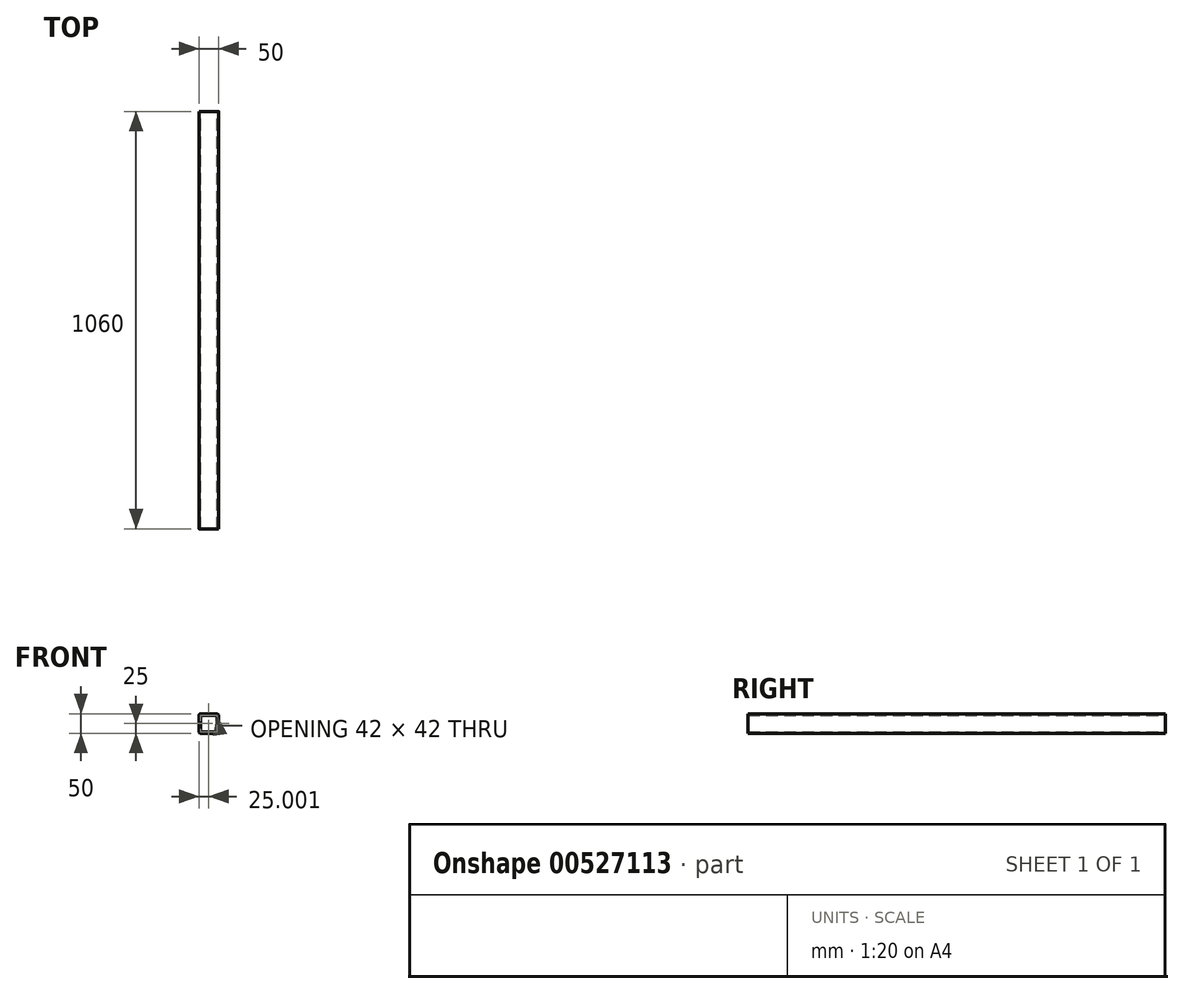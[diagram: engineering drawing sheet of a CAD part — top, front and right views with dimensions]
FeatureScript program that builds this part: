
annotation { "Feature Type Name" : "Feature", "Feature Type Description" : "" }
export const myFeature = defineFeature(function(context is Context, id is Id, definition is map)
    precondition{}
    {
        {
            var Q0;
            Q0=qCreatedBy(makeId("Front.planeOp"),FACE);
            var sketch = newSketch(context, id + "F0", { "sketchPlane" : qUnion([Q0])});
            skLineSegment(sketch, "E0.0", {"start": v(-14.7, 14) * mm, "end": v(5.3, 14) * mm});
            skLineSegment(sketch, "E1.0", {"start": v(-19.7, -31) * mm, "end": v(-19.7, 9) * mm});
            skLineSegment(sketch, "E2.0", {"start": v(-14.7, -36) * mm, "end": v(5.3, -36) * mm});
            skPoint(sketch, "E3.visualSharp", {"position": v(-19.7, -36) * mm});
            skArc(sketch, "E3.filletArc", {"start": v(-19.7, -31) * mm, "mid": v(-18.23, -34.54) * mm, "end": v(-14.7, -36) * mm});
            skPoint(sketch, "E4.visualSharp", {"position": v(-19.7, 14) * mm});
            skArc(sketch, "E4.filletArc", {"start": v(-14.7, 14) * mm, "mid": v(-18.23, 12.54) * mm, "end": v(-19.7, 9) * mm});
            skLineSegment(sketch, "E5", {"start": v(5.3, 14) * mm, "end": v(5.3, -38.2) * mm, "construction": true});
            skPoint(sketch, "E5.endSnap0", {"position": v(5.3, -36) * mm});
            skLineSegment(sketch, "E6.MirrorCS", {"start": v(25.3, 14) * mm, "end": v(5.3, 14) * mm});
            skArc(sketch, "E7.MirrorCS", {"start": v(25.3, 14) * mm, "mid": v(28.84, 12.54) * mm, "end": v(30.3, 9) * mm});
            skLineSegment(sketch, "E8.MirrorCS", {"start": v(30.3, -31) * mm, "end": v(30.3, 9) * mm});
            skArc(sketch, "E9.MirrorCS", {"start": v(30.3, -31) * mm, "mid": v(28.84, -34.54) * mm, "end": v(25.3, -36) * mm});
            skLineSegment(sketch, "E10.MirrorCS", {"start": v(25.3, -36) * mm, "end": v(5.3, -36) * mm});
            skLineSegment(sketch, "E11.0", {"start": v(-15.7, 10) * mm, "end": v(5.3, 10) * mm});
            skLineSegment(sketch, "E11.1", {"start": v(26.3, -32) * mm, "end": v(26.3, 10) * mm});
            skLineSegment(sketch, "E11.2", {"start": v(26.3, -32) * mm, "end": v(5.3, -32) * mm});
            skLineSegment(sketch, "E11.3", {"start": v(26.3, 10) * mm, "end": v(5.3, 10) * mm});
            skLineSegment(sketch, "E11.4", {"start": v(-15.7, -32) * mm, "end": v(5.3, -32) * mm});
            skLineSegment(sketch, "E11.5", {"start": v(-15.7, -32) * mm, "end": v(-15.7, 10) * mm});
            skSolve(sketch);
        }
        {
            var Q0;
            Q0 = qSketchRegion(id + "F0", true);
            extrude(context, id + "F1", {"entities" : qUnion([Q0]), "depth" : (1150 - 90) * mm, "offsetDistance" : 25 * mm});
        }
        {
            var Q0;
            Q0=makeQuery(id+"F1.opExtrude","SWEPT_EDGE",EDGE,{"disambiguationData":[OSD([sQuery(id+"F0.wireOp",EDGE,"E11.0"),sQuery(id+"F0.wireOp",EDGE,"E11.5")])]});
            var Q1;
            Q1=makeQuery(id+"F1.opExtrude","SWEPT_EDGE",EDGE,{"disambiguationData":[OSD([sQuery(id+"F0.wireOp",EDGE,"E11.1"),sQuery(id+"F0.wireOp",EDGE,"E11.3")])]});
            var Q2;
            Q2=makeQuery(id+"F1.opExtrude","SWEPT_EDGE",EDGE,{"disambiguationData":[OSD([sQuery(id+"F0.wireOp",EDGE,"E11.1"),sQuery(id+"F0.wireOp",EDGE,"E11.2")])]});
            var Q3;
            Q3=makeQuery(id+"F1.opExtrude","SWEPT_EDGE",EDGE,{"disambiguationData":[OSD([sQuery(id+"F0.wireOp",EDGE,"E11.4"),sQuery(id+"F0.wireOp",EDGE,"E11.5")])]});
            fillet(context, id + "F2", {"entities" : qUnion([Q0, Q1, Q2, Q3]), "radius" : 2 * mm, "allowEdgeOverflow" : false});
        }
    });
